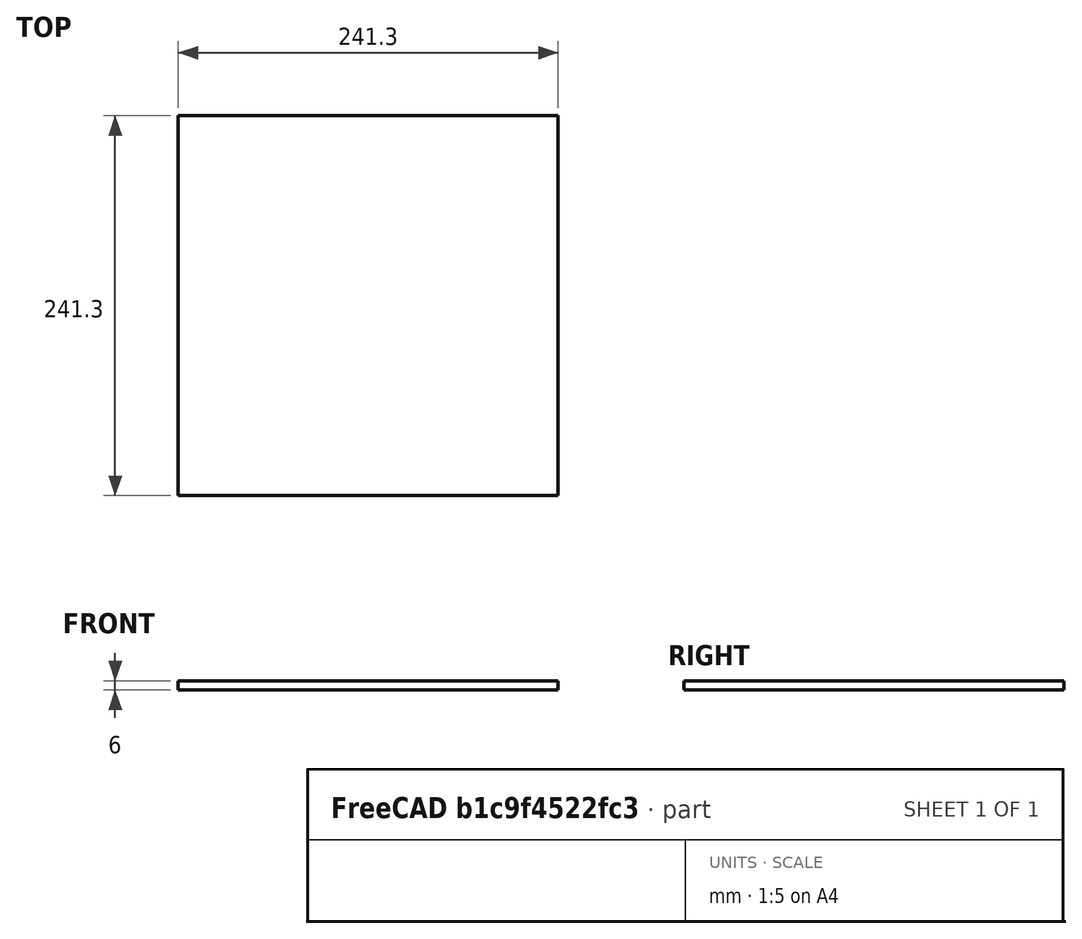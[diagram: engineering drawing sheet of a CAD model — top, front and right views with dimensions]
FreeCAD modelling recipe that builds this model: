
FCSTD DOCUMENT  (FreeCAD 0.21R33675 (Git))
Label: box_divider_no_slot
License: All rights reserved
LicenseURL: https://en.wikipedia.org/wiki/All_rights_reserved
objects: Spreadsheet::Sheet×1, Sketcher::SketchObject×1, PartDesign::Pad×1, PartDesign::Body×1
note: 4 computed .brp shape members not serialized (recipe doc carries the construction recipe); baked Part::Feature solids carry a one-line shape summary decoded from their .brp

FEATURE [Spreadsheet::Sheet] Spreadsheet
  cells = A2='Design Parameters; A3='width; B3(width)==9.5 in; A4='height; B4(height)==9.5 in; A5='thickness; B5(thickness)==6 mm
FEATURE [Sketcher::SketchObject] Sketch
  FullyConstrained = true
  MapMode = 5
  Support = -> [XY_Plane]
  expr: Constraints[10] = Spreadsheet.height
  expr: Constraints[11] = Spreadsheet.width
  sketch-geometry (5):
    g0: LineSegment StartX=-120.65 StartY=120.65 StartZ=0 EndX=-120.65 EndY=-120.65 EndZ=0
    g1: LineSegment StartX=-120.65 StartY=-120.65 StartZ=0 EndX=120.65 EndY=-120.65 EndZ=0
    g2: LineSegment StartX=120.65 StartY=-120.65 StartZ=0 EndX=120.65 EndY=120.65 EndZ=0
    g3: LineSegment StartX=120.65 StartY=120.65 StartZ=0 EndX=-120.65 EndY=120.65 EndZ=0
    g4: GeomPoint X=0 Y=0 Z=0
  constraints (12):
    c: Coincident(g0,g1)
    c: Coincident(g1,g2)
    c: Coincident(g2,g3)
    c: Coincident(g3,g0)
    c: Horizontal(g1)
    c: Horizontal(g3)
    c: Vertical(g0)
    c: Vertical(g2)
    c: Symmetric(g1,g0,g4)
    c: Coincident(g4,g-1)
    c: DistanceY(g2,g2) = 241.3
    c: DistanceX(g1,g1) = 241.3
FEATURE [PartDesign::Pad] Pad
  Direction = (0,0,1)
  Length = 6
  Length2 = 10
  Profile = -> Sketch
  ReferenceAxis = -> Sketch [N_Axis]
  Type = 0
  expr: Length = Spreadsheet.thickness
FEATURE [PartDesign::Body] Body
  Group = -> [Sketch,Pad]
  Origin = -> Origin
  Tip = -> Pad
